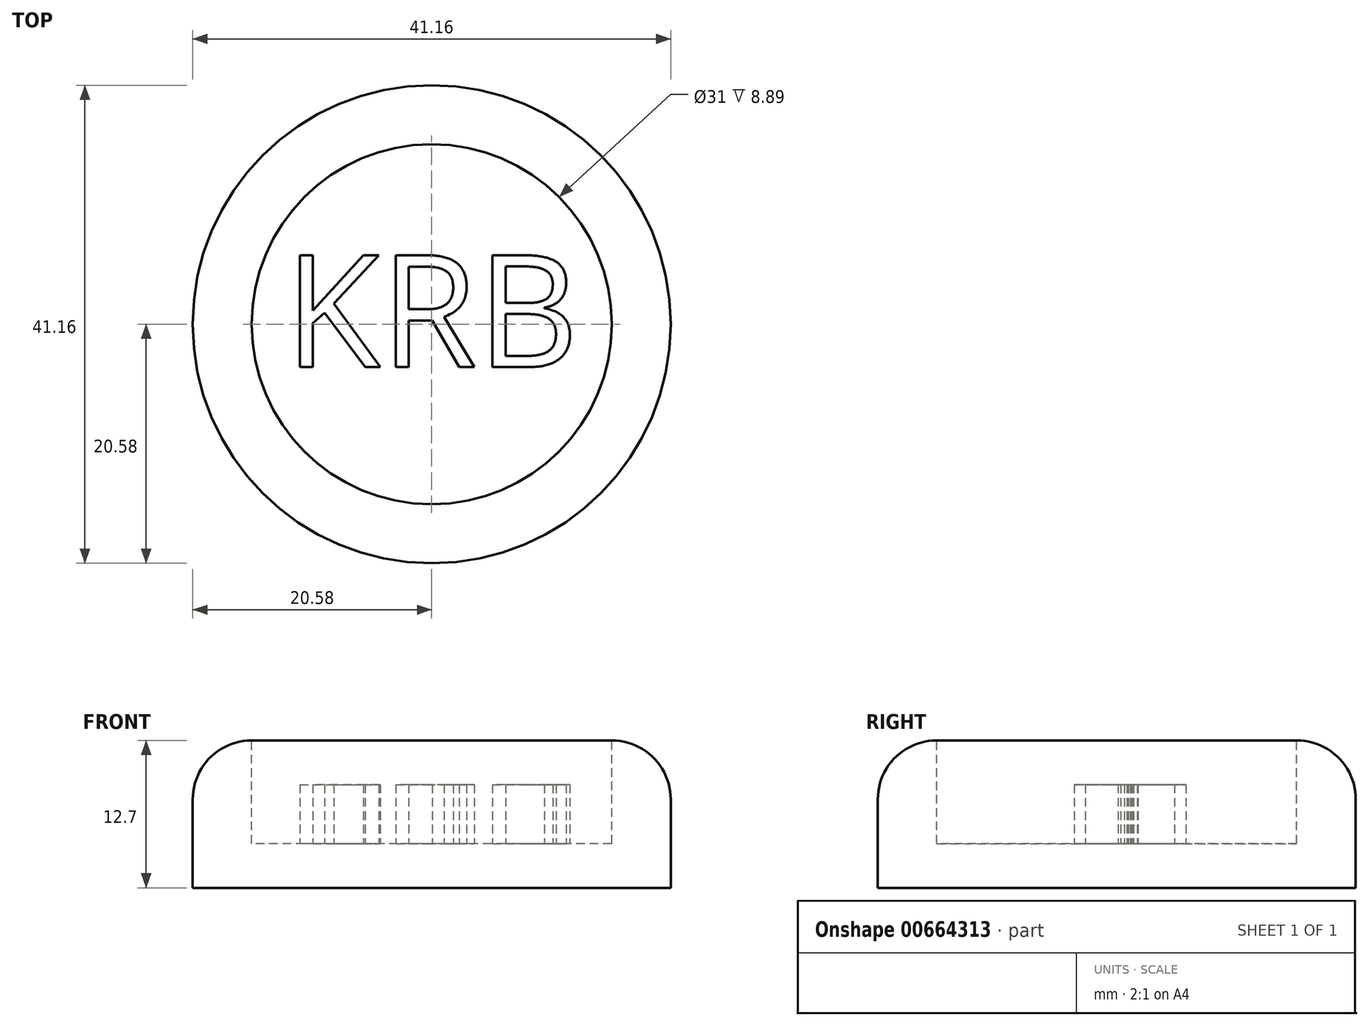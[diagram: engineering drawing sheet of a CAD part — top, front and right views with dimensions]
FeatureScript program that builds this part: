
annotation { "Feature Type Name" : "Feature", "Feature Type Description" : "" }
export const myFeature = defineFeature(function(context is Context, id is Id, definition is map)
    precondition{}
    {
        {
            var Q0;
            Q0=qCreatedBy(makeId("Top.planeOp"),FACE);
            var sketch = newSketch(context, id + "F0", { "sketchPlane" : qUnion([Q0])});
            skCircle(sketch, "E0", {"center": v(0, 0) * mm, "radius": 20.58 * mm});
            skSolve(sketch);
        }
        {
            var Q0;
            Q0=makeQuery(id+"F0.imprint","IMPRINT",FACE,{"disambiguationData":[TD([[makeQuery(id+"F0.imprint","IMPRINT",EDGE,{"derivedFrom":sQuery(id+"F0.wireOp",EDGE,"E0")}),1.0]])]});
            extrude(context, id + "F1", {"entities" : qUnion([Q0]), "depth" : 12.7 * mm, "offsetDistance" : 25.4 * mm});
        }
        {
            var Q0;
            Q0=qCreatedBy(makeId("Right.planeOp"),FACE);
            var sketch = newSketch(context, id + "F2", { "sketchPlane" : qUnion([Q0])});
            skLineSegment(sketch, "E1", {"start": v(0, 0) * mm, "end": v(0, -38.27) * mm});
            skSolve(sketch);
        }
        {
            var Q0;
            Q0=qCreatedBy(makeId("Front.planeOp"),FACE);
            var sketch = newSketch(context, id + "F3", { "sketchPlane" : qUnion([Q0])});
            skLineSegment(sketch, "E2", {"start": v(0, -38.33) * mm, "end": v(-20.38, 0) * mm});
            skSolve(sketch);
        }
        {
            var Q0;
            Q0=sQuery(id+"F3.wireOp",EDGE,"E2");
            var Q1;
            Q1=sQuery(id+"F2.wireOp",EDGE,"E1");
            revolve(context, id + "F4", {"bodyType" : ToolBodyType.SURFACE, "surfaceEntities" : qUnion([Q0]), "axis" : qUnion([Q1]), "revolveType" : RevolveType.FULL});
        }
        {
            var Q0;
            Q0=makeQuery(id+"F1.opExtrude","CAP_FACE",FACE,{"disambiguationData":[OSD([sQuery(id+"F0.wireOp",EDGE,"E0")])],"isStart":false});
            fillet(context, id + "F5", {"entities" : qUnion([Q0]), "radius" : 5.08 * mm, "tangentPropagation" : true, "allowEdgeOverflow" : false});
        }
        {
            var Q0;
            Q0=makeQuery(id+"F1.opExtrude","CAP_FACE",FACE,{"disambiguationData":[OSD([sQuery(id+"F0.wireOp",EDGE,"E0")])],"isStart":false});
            extrude(context, id + "F6", {"entities" : qUnion([Q0]), "operationType" : NewBodyOperationType.REMOVE, "oppositeDirection" : true, "depth" : 8.9 * mm, "offsetDistance" : 25.4 * mm});
        }
        {
            var Q0;
            Q0=makeQuery(id+"F6.boolean.opBoolean","COPY",FACE,{"derivedFrom":makeQuery(id+"F6.opExtrude","CAP_FACE",FACE,{"disambiguationData":[OSD([sQuery(id+"F0.wireOp",EDGE,"E0")])],"isStart":false})});
            var sketch = newSketch(context, id + "F7", { "sketchPlane" : qUnion([Q0])});
            skText(sketch, "E3", { "text": "KRB", "fontName": "OpenSans-Regular.ttf"});
            const initialGuessF7  = {"E3": [-0.01268, -0.00367, 1, 0, 0.0097]};
            skSetInitialGuess(sketch, initialGuessF7);
            skSolve(sketch);
        }
        {
            var Q0;
            Q0 = qSketchRegion(id + "F7", true);
            extrude(context, id + "F8", {"entities" : qUnion([Q0]), "operationType" : NewBodyOperationType.ADD, "depth" : 5.08 * mm, "offsetDistance" : 25.4 * mm});
        }
    });
